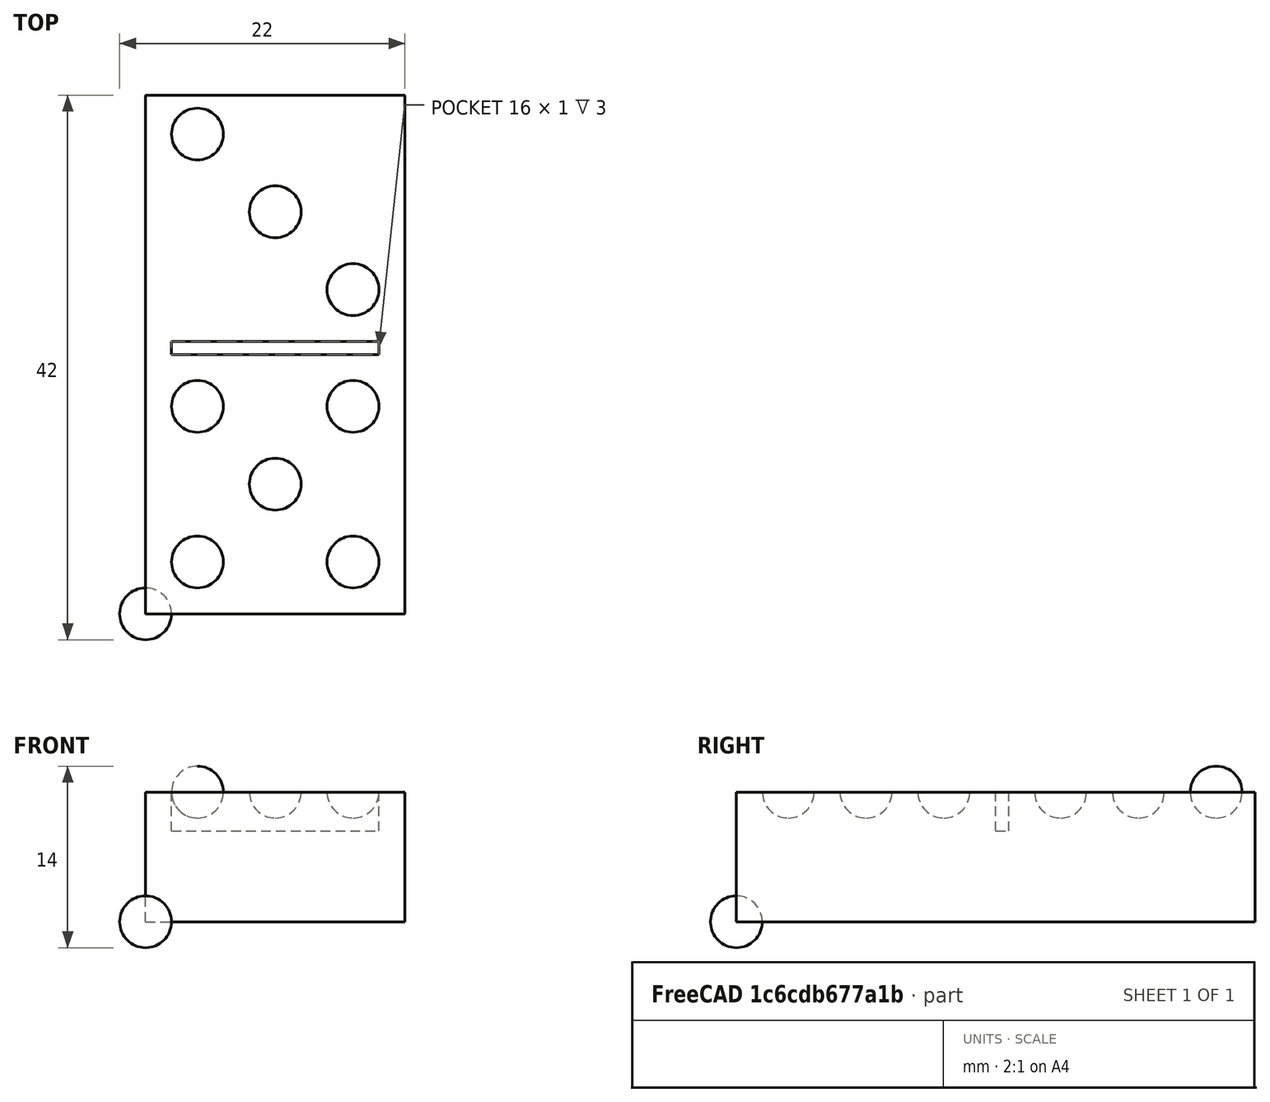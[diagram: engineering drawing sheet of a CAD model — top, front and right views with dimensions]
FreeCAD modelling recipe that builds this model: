
FCSTD DOCUMENT  (FreeCAD 0.21R33694 (Git))
Label: OJT1_T13R03_domino
License: All rights reserved
LicenseURL: http://en.wikipedia.org/wiki/All_rights_reserved
objects: Part::Cut×4, Part::Sphere×3, Part::Box×2, Part::FeaturePython×2
note: 9 computed .brp shape members not serialized (recipe doc carries the construction recipe); baked Part::Feature solids carry a one-line shape summary decoded from their .brp

FEATURE [Part::Box] Box  label="base"
  AttacherType = Attacher::AttachEngine3D
  Height = 10
  Length = 20
  Width = 40
FEATURE [Part::Box] Box001  label="Cube"
  AttacherType = Attacher::AttachEngine3D
  Height = 4
  Length = 16
  Placement = pos=(2,20,7) rot=(0,0,1;0rad)
  Width = 1
FEATURE [Part::Sphere] Sphere
  Angle1 = -90
  Angle2 = 90
  Angle3 = 360
  AttacherType = Attacher::AttachEngine3D
  Placement = pos=(4,37,10) rot=(0,0,1;0rad)
  Radius = 2
FEATURE [Part::FeaturePython] Array  label="numero3"  # Draft array (typed FeaturePython)
  AlwaysSyncPlacement = false
  Angle = 360
  ArrayType = 0
  Axis = (0,0,1)
  Base = -> Sphere
  Center = (0,0,0)
  Count = 3
  ExpandArray = false
  Fuse = false
  IntervalAxis = (0,0,0)
  IntervalX = (6,-6,0)
  IntervalY = (0,100,0)
  IntervalZ = (0,0,100)
  NumberCircles = 3
  NumberPolar = 5
  NumberX = 3
  NumberY = 1
  NumberZ = 1
  PlacementList = 3 placements: arithmetic series from (4,37,10) step (6,-6,0) to (16,25,10)
  RadialDistance = 50
  ScaleList = (3) [(1,1,1),(1,1,1),(1,1,1)]
  Symmetry = 1
  TangentialDistance = 25
FEATURE [Part::Sphere] Sphere001
  Angle1 = -90
  Angle2 = 90
  Angle3 = 360
  AttacherType = Attacher::AttachEngine3D
  Radius = 2
FEATURE [Part::FeaturePython] Array001  # Draft array (typed FeaturePython)
  AlwaysSyncPlacement = false
  Angle = 360
  ArrayType = 0
  Axis = (0,0,1)
  Base = -> Sphere001
  Center = (0,0,0)
  Count = 4
  ExpandArray = false
  Fuse = false
  IntervalAxis = (0,0,0)
  IntervalX = (12,0,0)
  IntervalY = (0,12,0)
  IntervalZ = (0,0,100)
  NumberCircles = 3
  NumberPolar = 5
  NumberX = 2
  NumberY = 2
  NumberZ = 1
  Placement = pos=(4,4,10) rot=(0,0,1;0rad)
  PlacementList = 4 placements: [(0,0,0),(0,12,0),(12,0,0),(12,12,0)]
  RadialDistance = 50
  ScaleList = (4) [(1,1,1),(1,1,1),(1,1,1),(1,1,1)]
  Symmetry = 1
  TangentialDistance = 25
FEATURE [Part::Sphere] Sphere002
  Angle1 = -90
  Angle2 = 90
  Angle3 = 360
  AttacherType = Attacher::AttachEngine3D
  Placement = pos=(10,10,10) rot=(0,0,1;0rad)
  Radius = 2
FEATURE [Part::Cut] Cut
  Base = -> Box
  Refine = true
  Tool = -> Box001
FEATURE [Part::Cut] Cut001
  Base = -> Cut
  Refine = true
  Tool = -> Sphere002
FEATURE [Part::Cut] Cut002
  Base = -> Cut001
  Refine = true
  Tool = -> Array001
FEATURE [Part::Cut] Cut003
  Base = -> Cut002
  Refine = true
  Tool = -> Array
